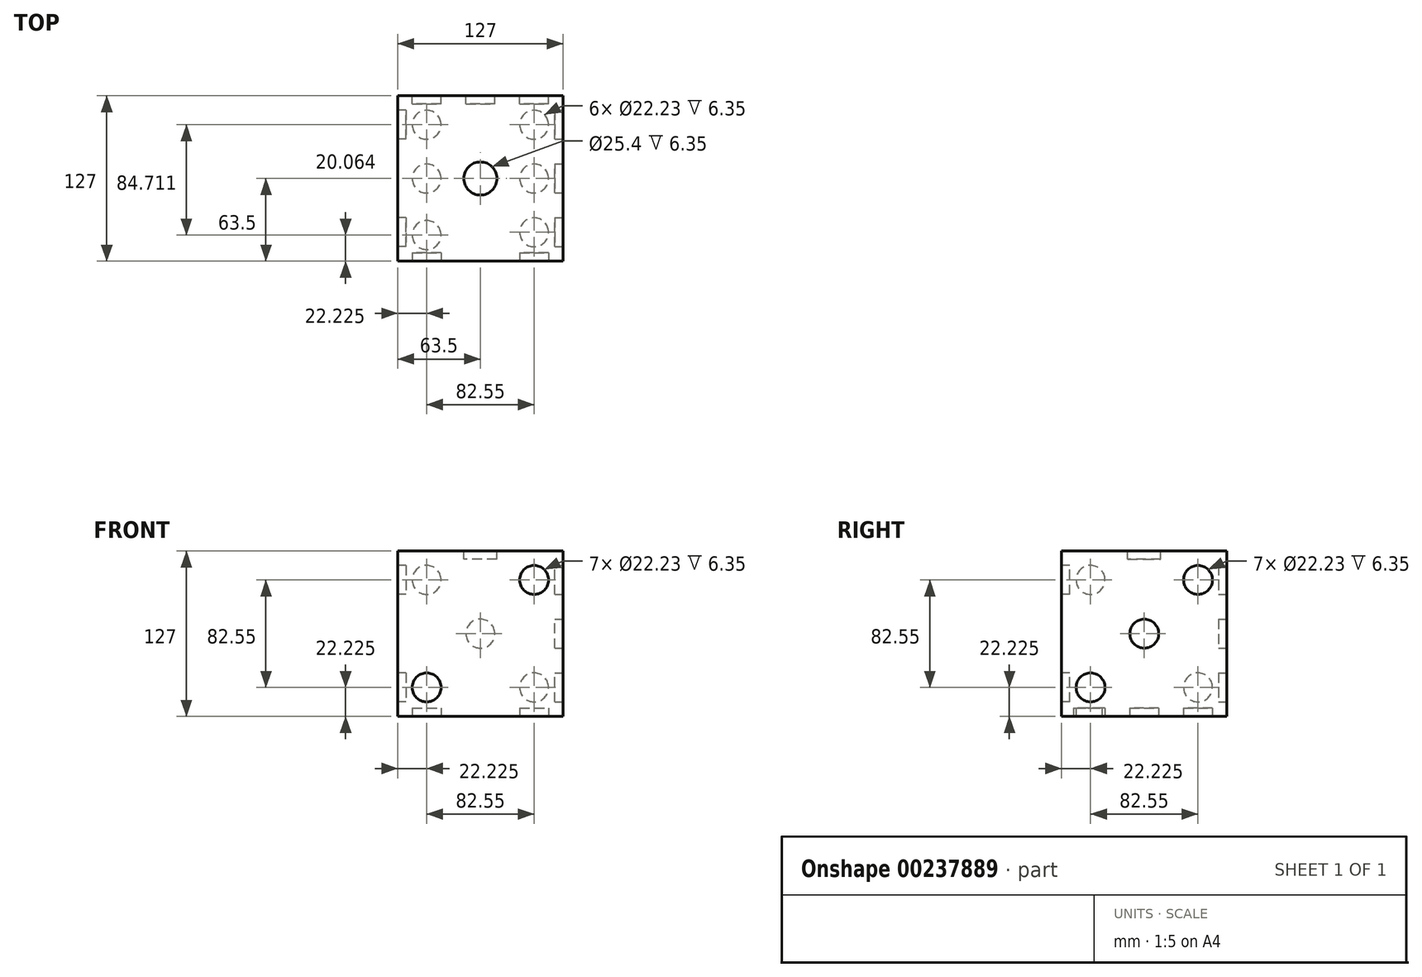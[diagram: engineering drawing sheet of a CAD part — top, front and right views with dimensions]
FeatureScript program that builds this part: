
annotation { "Feature Type Name" : "Feature", "Feature Type Description" : "" }
export const myFeature = defineFeature(function(context is Context, id is Id, definition is map)
    precondition{}
    {
        {
            var Q0;
            Q0=qCreatedBy(makeId("Top.planeOp"),FACE);
            var sketch = newSketch(context, id + "F0", { "sketchPlane" : qUnion([Q0])});
            skLineSegment(sketch, "E0.bottom", {"start": v(0, 0) * mm, "end": v(127, 0) * mm});
            skLineSegment(sketch, "E0.top", {"start": v(0, 127) * mm, "end": v(127, 127) * mm});
            skLineSegment(sketch, "E0.left", {"start": v(0, 0) * mm, "end": v(0, 127) * mm});
            skLineSegment(sketch, "E0.right", {"start": v(127, 0) * mm, "end": v(127, 127) * mm});
            skSolve(sketch);
        }
        {
            var Q0;
            Q0 = qSketchRegion(id + "F0", true);
            extrude(context, id + "F1", {"entities" : qUnion([Q0]), "depth" : 127 * mm});
        }
        {
            var Q0;
            Q0=makeQuery(id+"F1.opExtrude","CAP_FACE",FACE,{"disambiguationData":[OSD([sQuery(id+"F0.wireOp",EDGE,"E0.bottom"),sQuery(id+"F0.wireOp",EDGE,"E0.top"),sQuery(id+"F0.wireOp",EDGE,"E0.left"),sQuery(id+"F0.wireOp",EDGE,"E0.right")])],"isStart":false});
            var sketch = newSketch(context, id + "F2", { "sketchPlane" : qUnion([Q0])});
            skCircle(sketch, "E1", {"center": v(63.5, 63.5) * mm, "radius": 12.7 * mm});
            skPoint(sketch, "E1.centerSnap0", {"position": v(127, 63.5) * mm});
            skPoint(sketch, "E1.centerSnap1", {"position": v(63.5, 127) * mm});
            skSolve(sketch);
        }
        {
            var Q0;
            Q0 = qSketchRegion(id + "F2", true);
            extrude(context, id + "F3", {"entities" : qUnion([Q0]), "operationType" : NewBodyOperationType.REMOVE, "oppositeDirection" : true, "depth" : 6.35 * mm});
        }
        {
            var Q0;
            Q0=makeQuery(id+"F1.opExtrude","SWEPT_FACE",FACE,{"disambiguationData":[OSD([sQuery(id+"F0.wireOp",EDGE,"E0.bottom")])]});
            var sketch = newSketch(context, id + "F4", { "sketchPlane" : qUnion([Q0])});
            skCircle(sketch, "E2", {"center": v(22.23, 22.22) * mm, "radius": 11.11 * mm});
            skCircle(sketch, "E3", {"center": v(104.78, 104.78) * mm, "radius": 11.11 * mm});
            skSolve(sketch);
        }
        {
            var Q0;
            Q0 = qSketchRegion(id + "F4", true);
            extrude(context, id + "F5", {"entities" : qUnion([Q0]), "operationType" : NewBodyOperationType.REMOVE, "oppositeDirection" : true, "depth" : 6.35 * mm});
        }
        {
            var Q0;
            Q0=makeQuery(id+"F1.opExtrude","SWEPT_FACE",FACE,{"disambiguationData":[OSD([sQuery(id+"F0.wireOp",EDGE,"E0.right")])]});
            var sketch = newSketch(context, id + "F6", { "sketchPlane" : qUnion([Q0])});
            skLineSegment(sketch, "E4", {"start": v(0, 0) * mm, "end": v(127, 127) * mm, "construction": true});
            skCircle(sketch, "E5", {"center": v(63.5, 63.5) * mm, "radius": 11.11 * mm});
            skCircle(sketch, "E6", {"center": v(22.22, 22.23) * mm, "radius": 11.11 * mm});
            skCircle(sketch, "E7", {"center": v(104.77, 104.78) * mm, "radius": 11.11 * mm});
            skSolve(sketch);
        }
        {
            var Q0;
            Q0 = qSketchRegion(id + "F6", true);
            extrude(context, id + "F7", {"entities" : qUnion([Q0]), "operationType" : NewBodyOperationType.REMOVE, "oppositeDirection" : true, "depth" : 6.35 * mm});
        }
        {
            var Q0;
            Q0=makeQuery(id+"F1.opExtrude","SWEPT_FACE",FACE,{"disambiguationData":[OSD([sQuery(id+"F0.wireOp",EDGE,"E0.left")])]});
            var sketch = newSketch(context, id + "F8", { "sketchPlane" : qUnion([Q0])});
            skCircle(sketch, "E8", {"center": v(-104.78, 104.78) * mm, "radius": 11.11 * mm});
            skCircle(sketch, "E9", {"center": v(-104.78, 22.22) * mm, "radius": 11.11 * mm});
            skCircle(sketch, "E10", {"center": v(-22.23, 104.78) * mm, "radius": 11.11 * mm});
            skCircle(sketch, "E11", {"center": v(-22.23, 22.22) * mm, "radius": 11.11 * mm});
            skSolve(sketch);
        }
        {
            var Q0;
            Q0 = qSketchRegion(id + "F8", true);
            extrude(context, id + "F9", {"entities" : qUnion([Q0]), "operationType" : NewBodyOperationType.REMOVE, "oppositeDirection" : true, "depth" : 6.35 * mm});
        }
        {
            var Q0;
            Q0=makeQuery(id+"F1.opExtrude","SWEPT_FACE",FACE,{"disambiguationData":[OSD([sQuery(id+"F0.wireOp",EDGE,"E0.top")])]});
            var sketch = newSketch(context, id + "F10", { "sketchPlane" : qUnion([Q0])});
            skCircle(sketch, "E12", {"center": v(-63.5, 63.5) * mm, "radius": 11.11 * mm});
            skPoint(sketch, "E12.centerSnap0", {"position": v(0, 63.5) * mm});
            skPoint(sketch, "E12.centerSnap1", {"position": v(-63.5, 127) * mm});
            skCircle(sketch, "E13", {"center": v(-104.77, 104.78) * mm, "radius": 11.11 * mm});
            skCircle(sketch, "E14", {"center": v(-22.23, 104.78) * mm, "radius": 11.11 * mm});
            skCircle(sketch, "E15", {"center": v(-22.23, 22.22) * mm, "radius": 11.11 * mm});
            skCircle(sketch, "E16", {"center": v(-104.77, 22.22) * mm, "radius": 11.11 * mm});
            skSolve(sketch);
        }
        {
            var Q0;
            Q0=makeQuery(id+"F10.imprint","IMPRINT",FACE,{"disambiguationData":[TD([[makeQuery(id+"F10.imprint","IMPRINT",EDGE,{"derivedFrom":sQuery(id+"F10.wireOp",EDGE,"E13")}),1.0]])]});
            var Q1;
            Q1=makeQuery(id+"F10.imprint","IMPRINT",FACE,{"disambiguationData":[TD([[makeQuery(id+"F10.imprint","IMPRINT",EDGE,{"derivedFrom":sQuery(id+"F10.wireOp",EDGE,"E12")}),1.0]])]});
            var Q2;
            Q2=makeQuery(id+"F10.imprint","IMPRINT",FACE,{"disambiguationData":[TD([[makeQuery(id+"F10.imprint","IMPRINT",EDGE,{"derivedFrom":sQuery(id+"F10.wireOp",EDGE,"E15")}),1.0]])]});
            var Q3;
            Q3=makeQuery(id+"F10.imprint","IMPRINT",FACE,{"disambiguationData":[TD([[makeQuery(id+"F10.imprint","IMPRINT",EDGE,{"derivedFrom":sQuery(id+"F10.wireOp",EDGE,"E16")}),1.0]])]});
            var Q4;
            Q4=makeQuery(id+"F10.imprint","IMPRINT",FACE,{"disambiguationData":[TD([[makeQuery(id+"F10.imprint","IMPRINT",EDGE,{"derivedFrom":sQuery(id+"F10.wireOp",EDGE,"E14")}),1.0]])]});
            extrude(context, id + "F11", {"entities" : qUnion([Q0, Q1, Q2, Q3, Q4]), "operationType" : NewBodyOperationType.REMOVE, "oppositeDirection" : true, "depth" : 6.35 * mm});
        }
        {
            var Q0;
            Q0=makeQuery(id+"F1.opExtrude","CAP_FACE",FACE,{"disambiguationData":[OSD([sQuery(id+"F0.wireOp",EDGE,"E0.bottom"),sQuery(id+"F0.wireOp",EDGE,"E0.top"),sQuery(id+"F0.wireOp",EDGE,"E0.left"),sQuery(id+"F0.wireOp",EDGE,"E0.right")])],"isStart":true});
            var sketch = newSketch(context, id + "F12", { "sketchPlane" : qUnion([Q0])});
            skCircle(sketch, "E17", {"center": v(104.77, -104.78) * mm, "radius": 11.11 * mm});
            skCircle(sketch, "E18", {"center": v(104.78, -63.5) * mm, "radius": 11.11 * mm});
            skPoint(sketch, "E18.centerSnap0", {"position": v(127, -63.5) * mm});
            skCircle(sketch, "E19", {"center": v(104.78, -22.23) * mm, "radius": 11.11 * mm});
            skCircle(sketch, "E20", {"center": v(22.23, -63.5) * mm, "radius": 11.11 * mm});
            skPoint(sketch, "E20.centerSnap0", {"position": v(0, -63.5) * mm});
            skCircle(sketch, "E21", {"center": v(22.23, -104.78) * mm, "radius": 11.11 * mm});
            skCircle(sketch, "E22", {"center": v(22.23, -20.06) * mm, "radius": 11.11 * mm});
            skSolve(sketch);
        }
        {
            var Q0;
            Q0 = qSketchRegion(id + "F12", true);
            extrude(context, id + "F13", {"entities" : qUnion([Q0]), "operationType" : NewBodyOperationType.REMOVE, "oppositeDirection" : true, "depth" : 6.35 * mm});
        }
    });
